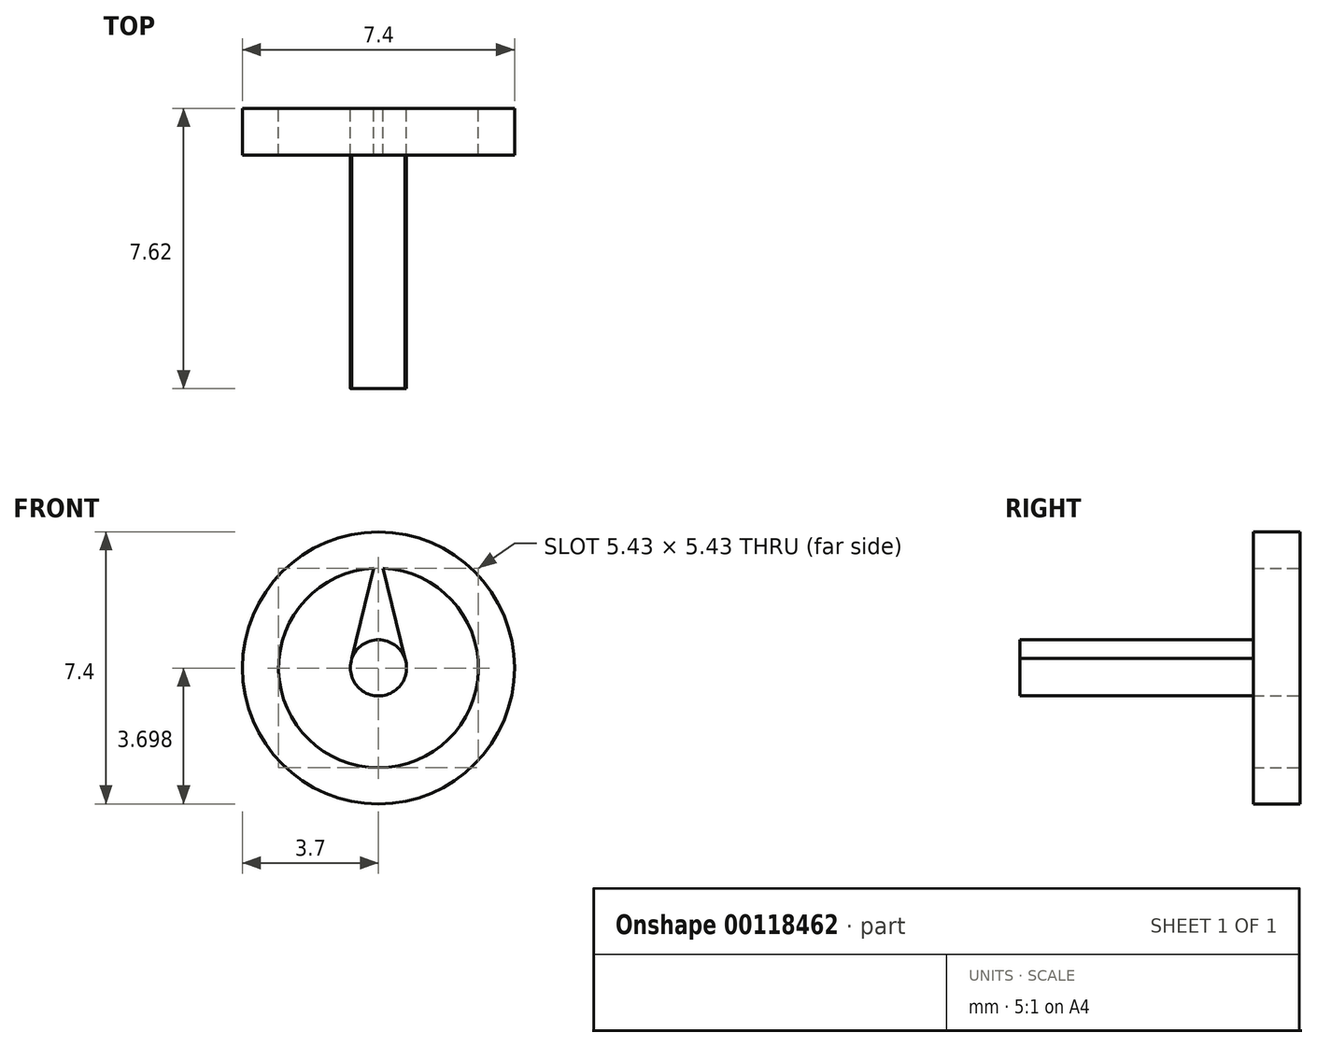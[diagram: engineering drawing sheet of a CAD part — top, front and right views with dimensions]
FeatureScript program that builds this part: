
annotation { "Feature Type Name" : "Feature", "Feature Type Description" : "" }
export const myFeature = defineFeature(function(context is Context, id is Id, definition is map)
    precondition{}
    {
        {
            var Q0;
            Q0=qCreatedBy(makeId("Front.planeOp"),FACE);
            var sketch = newSketch(context, id + "F0", { "sketchPlane" : qUnion([Q0])});
            skCircle(sketch, "E0", {"center": v(0, 0) * mm, "radius": 3.7 * mm});
            skArc(sketch, "E1", {"start": v(-0.13, 2.71) * mm, "mid": v(0, -2.72) * mm, "end": v(0.13, 2.71) * mm});
            skPoint(sketch, "E2.orphan", {"position": v(0, 3.27) * mm});
            skArc(sketch, "E3", {"start": v(-0.76, 0) * mm, "mid": v(0, -0.76) * mm, "end": v(0.76, 0) * mm});
            skArc(sketch, "E4", {"start": v(-0.74, 0.18) * mm, "mid": v(0, -0.76) * mm, "end": v(0.74, 0.18) * mm});
            skLineSegment(sketch, "E5", {"start": v(0.13, 2.71) * mm, "end": v(0.74, 0.18) * mm});
            skLineSegment(sketch, "E6", {"start": v(-0.13, 2.71) * mm, "end": v(-0.74, 0.18) * mm});
            skSolve(sketch);
        }
        {
            var Q0;
            Q0=makeQuery(id+"F0.imprint","IMPRINT",FACE,{"disambiguationData":[TD([[makeQuery(id+"F0.imprint","IMPRINT",EDGE,{"derivedFrom":sQuery(id+"F0.wireOp",EDGE,"E0")}),1.0]])]});
            extrude(context, id + "F1", {"entities" : qUnion([Q0]), "depth" : 1.27 * mm});
        }
        {
            var Q0;
            Q0=makeQuery(id+"F1.opExtrude","CAP_FACE",FACE,{"disambiguationData":[OSD([sQuery(id+"F0.wireOp",EDGE,"E0"),sQuery(id+"F0.wireOp",EDGE,"E1"),sQuery(id+"F0.wireOp",EDGE,"E4"),sQuery(id+"F0.wireOp",EDGE,"E5"),sQuery(id+"F0.wireOp",EDGE,"E6")])],"isStart":false});
            var sketch = newSketch(context, id + "F2", { "sketchPlane" : qUnion([Q0])});
            skCircle(sketch, "E7", {"center": v(0, 0) * mm, "radius": 0.77 * mm});
            skSolve(sketch);
        }
        {
            var Q0;
            {var subQ5=makeQuery(id+"F1.opExtrude","CAP_EDGE",EDGE,{"disambiguationData":[OSD([sQuery(id+"F0.wireOp",EDGE,"E4")])],"isStart":false});Q0=makeQuery(id+"F2.imprint","IMPRINT",FACE,{"disambiguationData":[TD([[makeQuery(id+"F2.imprint","IMPRINT",EDGE,{"derivedFrom":subQ5}),1.0]])]});}
            extrude(context, id + "F3", {"entities" : qUnion([Q0]), "operationType" : NewBodyOperationType.ADD, "depth" : 6.35 * mm});
        }
    });
